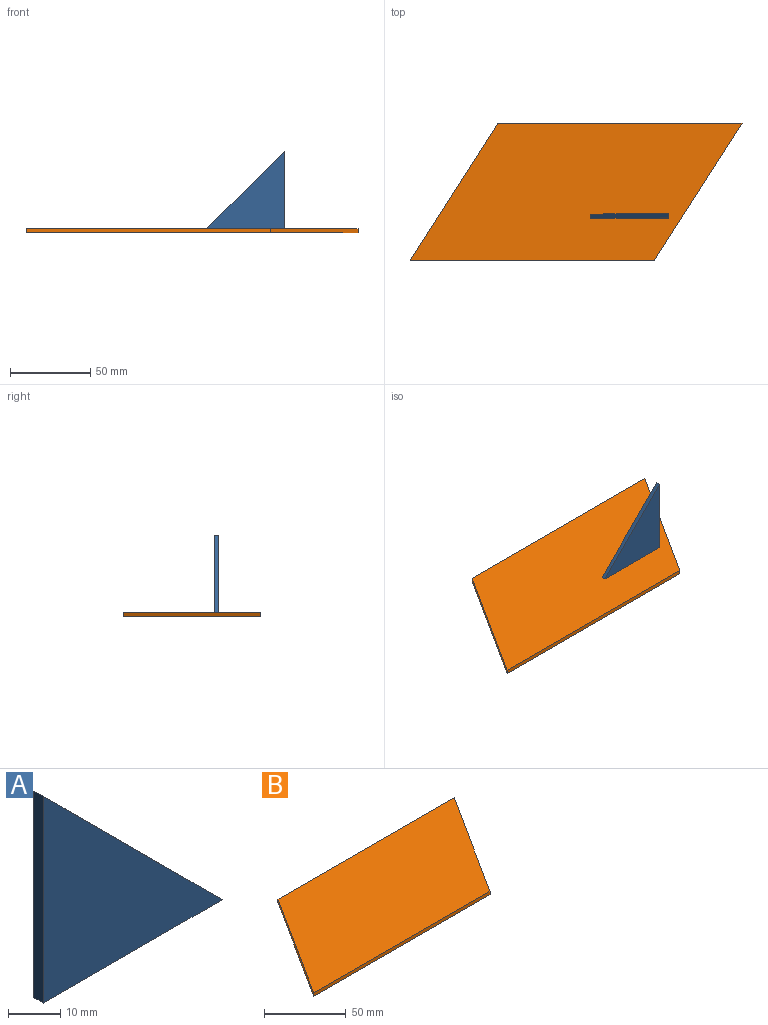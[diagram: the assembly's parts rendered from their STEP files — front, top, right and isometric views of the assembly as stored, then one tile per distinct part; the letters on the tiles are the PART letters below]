
ASSEMBLY  parts=2 mates=1
PART A: 5 faces, bbox 48.3x2.5x48.3 mm
  f0: plane 48.26x48.26mm, normal (0.71,0,0.71), area 173.4mm2, adj f1,f2,f3,f4
  f1: plane 48.26x2.54mm, normal (-1,0,0), area 122.6mm2, adj f0,f2,f3,f4
  f2: plane 48.26x2.54mm, normal (0,0,-1), area 122.6mm2, adj f0,f1,f3,f4
  f3: plane 48.26x48.26mm, normal (0,-1,0), area 1164.5mm2, adj f0,f1,f2
  f4: plane 48.26x48.26mm, normal (0,1,0), area 1164.5mm2, adj f0,f1,f2
PART B: 6 faces, bbox 207.3x85.8x2.5 mm
  f0: plane 152.4x2.54mm, normal (0,1,0), area 387.1mm2, adj f1,f3,f4,f5
  f1: plane 85.83x54.87mm, normal (-0.84,0.54,0), area 258.8mm2, adj f0,f2,f4,f5
  f2: plane 152.4x2.54mm, normal (0,-1,0), area 387.1mm2, adj f1,f3,f4,f5
  f3: plane 85.83x54.87mm, normal (0.84,-0.54,0), area 258.8mm2, adj f0,f2,f4,f5
  f4: plane 207.27x85.83mm, normal (0,0,1), area 13081.2mm2, adj f0,f1,f2,f3
  f5: plane 207.27x85.83mm, normal (0,0,-1), area 13081.2mm2, adj f0,f1,f2,f3
PLACE A rot(axis=(0,0,1),180deg) t=(11.17,-7.86,-0.68)mm
PLACE B at identity
MATE fastened A.f2 <-> B.f4  axis (0,0,-1) through (45.87,-6.59,2.54)mm
